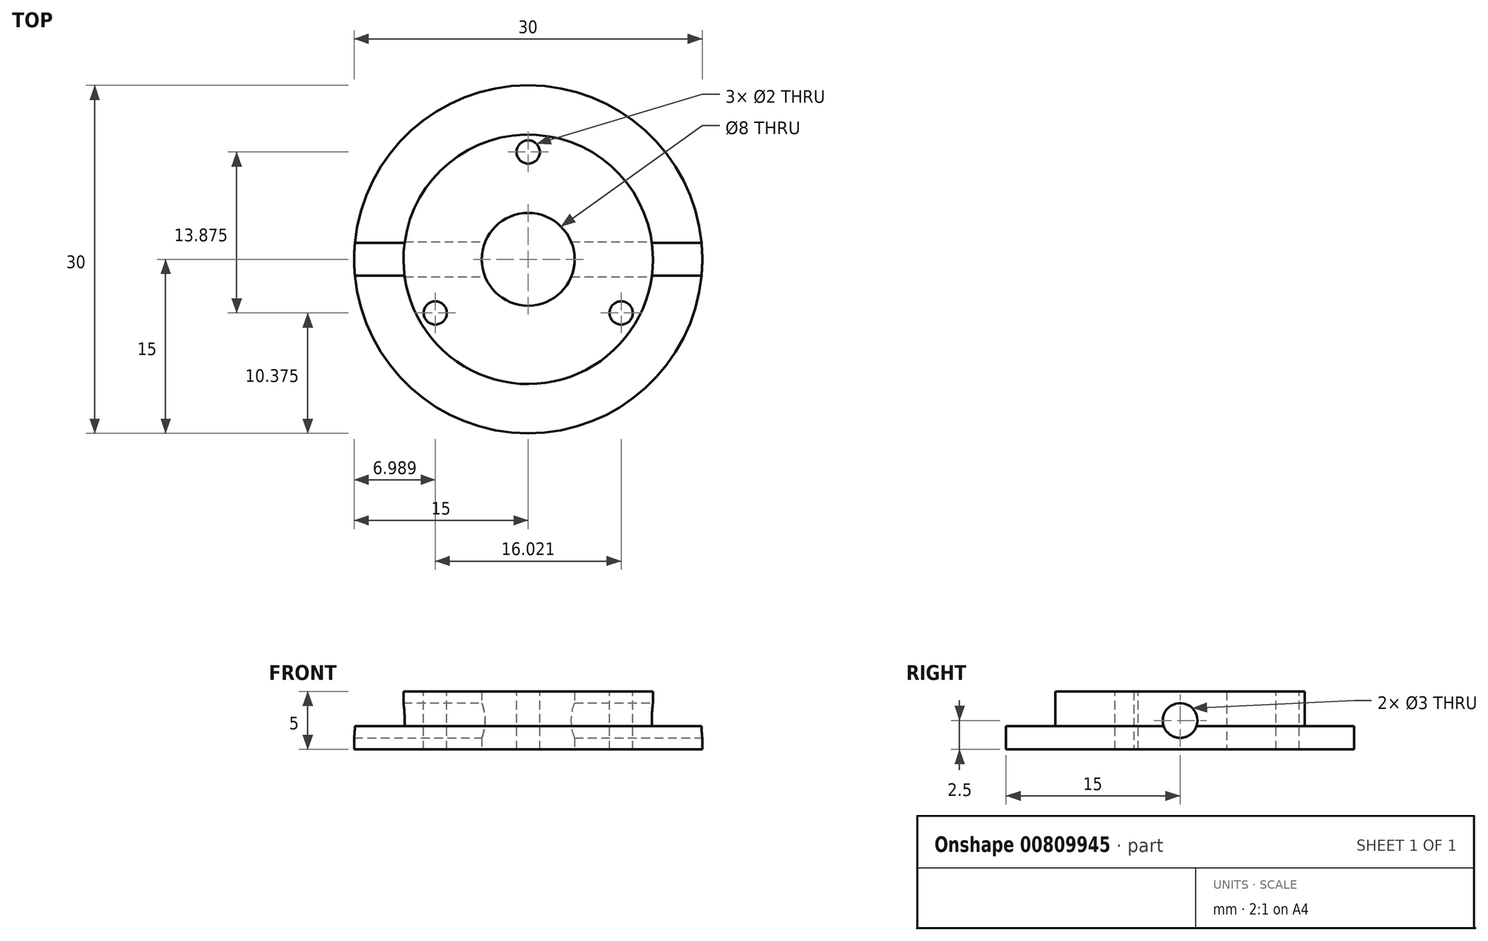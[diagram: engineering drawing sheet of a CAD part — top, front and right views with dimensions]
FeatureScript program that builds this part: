
annotation { "Feature Type Name" : "Feature", "Feature Type Description" : "" }
export const myFeature = defineFeature(function(context is Context, id is Id, definition is map)
    precondition{}
    {
        {
            var Q0;
            Q0=qCreatedBy(makeId("Top.planeOp"),FACE);
            var sketch = newSketch(context, id + "F0", { "sketchPlane" : qUnion([Q0])});
            skCircle(sketch, "E0", {"center": v(0, 0) * mm, "radius": 15 * mm});
            skCircle(sketch, "E1", {"center": v(0, 0) * mm, "radius": 4 * mm});
            skPoint(sketch, "E2", {"position": v(0, -15) * mm});
            skSolve(sketch);
        }
        {
            var Q0;
            Q0=makeQuery(id+"F0.imprint","IMPRINT",FACE,{"disambiguationData":[TD([[makeQuery(id+"F0.imprint","IMPRINT",EDGE,{"derivedFrom":sQuery(id+"F0.wireOp",EDGE,"E0")}),1.0]])]});
            extrude(context, id + "F1", {"entities" : qUnion([Q0]), "depth" : 2 * mm, "offsetDistance" : 25 * mm});
        }
        {
            var Q0;
            Q0=makeQuery(id+"F1.opExtrude","CAP_FACE",FACE,{"disambiguationData":[OSD([sQuery(id+"F0.wireOp",EDGE,"E0"),sQuery(id+"F0.wireOp",EDGE,"E1")])],"isStart":false});
            var sketch = newSketch(context, id + "F2", { "sketchPlane" : qUnion([Q0])});
            skCircle(sketch, "E3", {"center": v(0, 0) * mm, "radius": 10.75 * mm});
            skSolve(sketch);
        }
        {
            var Q0;
            Q0=makeQuery(id+"F2.imprint","IMPRINT",FACE,{"disambiguationData":[TD([[makeQuery(id+"F2.imprint","IMPRINT",EDGE,{"derivedFrom":sQuery(id+"F2.wireOp",EDGE,"E3")}),1.0]])]});
            extrude(context, id + "F3", {"entities" : qUnion([Q0]), "operationType" : NewBodyOperationType.ADD, "depth" : 3 * mm, "offsetDistance" : 25 * mm});
        }
        {
            var Q0;
            Q0=qCreatedBy(makeId("Right.planeOp"),FACE);
            var sketch = newSketch(context, id + "F4", { "sketchPlane" : qUnion([Q0])});
            skCircle(sketch, "E4", {"center": v(0, 2.5) * mm, "radius": 1.5 * mm});
            skSolve(sketch);
        }
        {
            var Q0;
            Q0=makeQuery(id+"F4.imprint","IMPRINT",FACE,{"disambiguationData":[TD([[makeQuery(id+"F4.imprint","IMPRINT",EDGE,{"derivedFrom":sQuery(id+"F4.wireOp",EDGE,"E4")}),1.0]])]});
            extrude(context, id + "F5", {"entities" : qUnion([Q0]), "operationType" : NewBodyOperationType.REMOVE, "oppositeDirection" : true, "depth" : 25 * mm, "offsetDistance" : 25 * mm, "hasSecondDirection" : true, "secondDirectionOppositeDirection" : false, "secondDirectionDepth" : 25 * mm});
        }
        {
            var Q0;
            Q0=makeQuery(id+"F3.opExtrude","CAP_FACE",FACE,{"disambiguationData":[OSD([sQuery(id+"F0.wireOp",EDGE,"E1"),sQuery(id+"F2.wireOp",EDGE,"E3")])],"isStart":false});
            var sketch = newSketch(context, id + "F6", { "sketchPlane" : qUnion([Q0])});
            skCircle(sketch, "E5", {"center": v(0, 9.25) * mm, "radius": 1 * mm});
            skCircle(sketch, "E6.1.0", {"center": v(8.01, -4.63) * mm, "radius": 1 * mm});
            skCircle(sketch, "E6.2.0", {"center": v(-8.01, -4.62) * mm, "radius": 1 * mm});
            skPoint(sketch, "E6.center", {"position": v(0, 0) * mm});
            skLineSegment(sketch, "E6.anchor1", {"start": v(0, 0) * mm, "end": v(0, 9.25) * mm, "construction": true});
            skLineSegment(sketch, "E6.anchor2", {"start": v(0, 0) * mm, "end": v(-8.01, -4.62) * mm, "construction": true});
            skSolve(sketch);
        }
        {
            var Q0;
            Q0=makeQuery(id+"F6.imprint","IMPRINT",FACE,{"disambiguationData":[TD([[makeQuery(id+"F6.imprint","IMPRINT",EDGE,{"derivedFrom":sQuery(id+"F6.wireOp",EDGE,"E6.1.0")}),1.0]])]});
            var Q1;
            Q1=makeQuery(id+"F6.imprint","IMPRINT",FACE,{"disambiguationData":[TD([[makeQuery(id+"F6.imprint","IMPRINT",EDGE,{"derivedFrom":sQuery(id+"F6.wireOp",EDGE,"E5")}),1.0]])]});
            var Q2;
            Q2=makeQuery(id+"F6.imprint","IMPRINT",FACE,{"disambiguationData":[TD([[makeQuery(id+"F6.imprint","IMPRINT",EDGE,{"derivedFrom":sQuery(id+"F6.wireOp",EDGE,"E6.2.0")}),1.0]])]});
            extrude(context, id + "F7", {"entities" : qUnion([Q0, Q1, Q2]), "operationType" : NewBodyOperationType.REMOVE, "oppositeDirection" : true, "depth" : 25 * mm, "offsetDistance" : 25 * mm});
        }
    });
